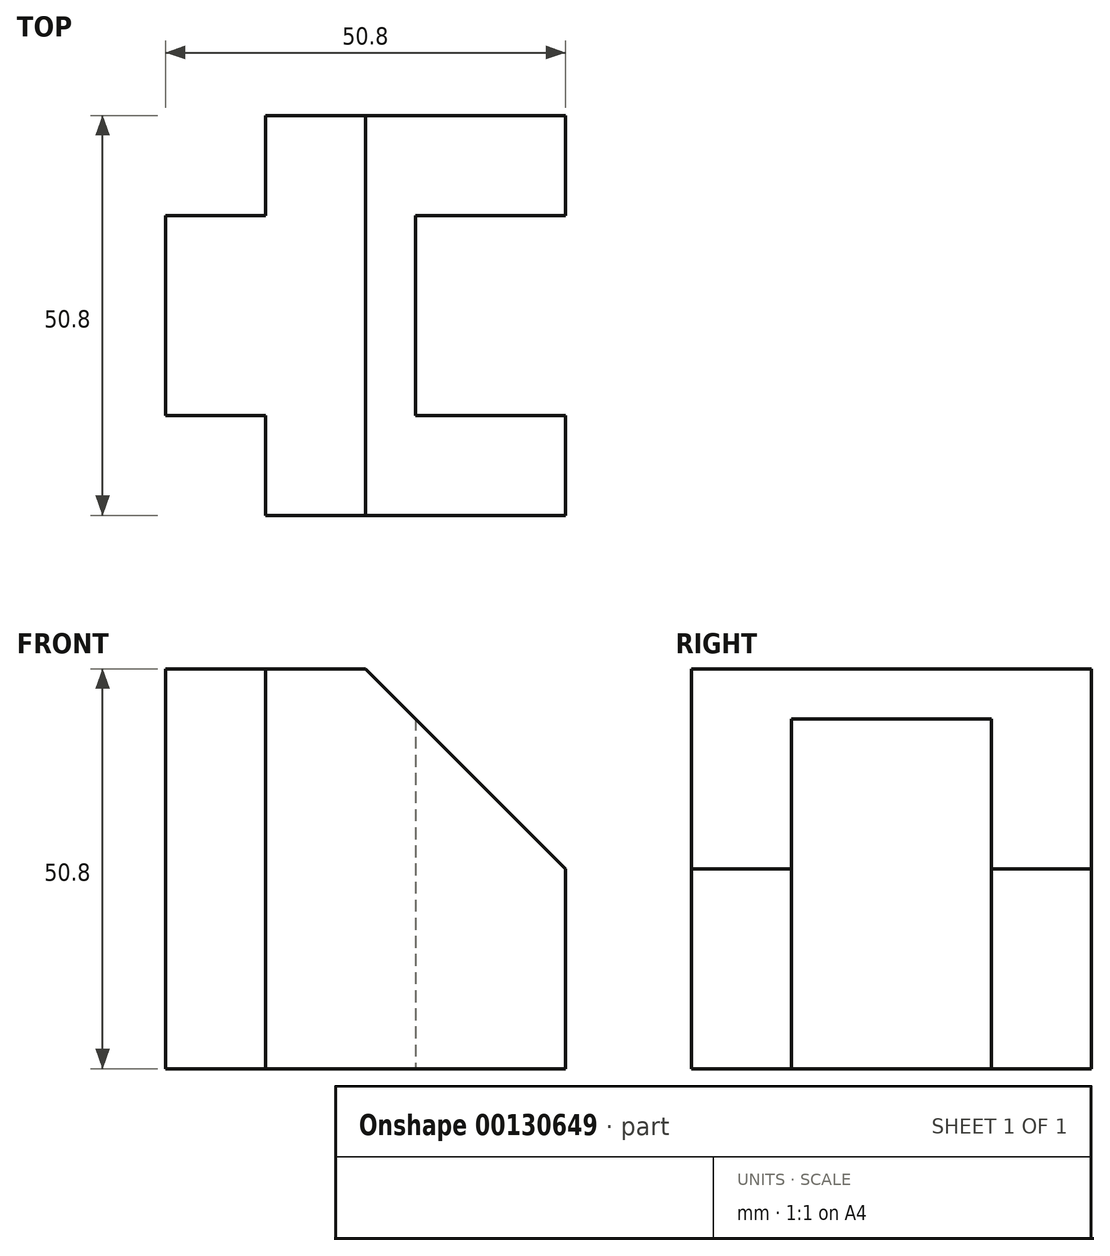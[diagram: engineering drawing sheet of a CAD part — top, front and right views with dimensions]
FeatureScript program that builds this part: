
annotation { "Feature Type Name" : "Feature", "Feature Type Description" : "" }
export const myFeature = defineFeature(function(context is Context, id is Id, definition is map)
    precondition{}
    {
        {
            var Q0;
            Q0=qCreatedBy(makeId("Front.planeOp"),FACE);
            var sketch = newSketch(context, id + "F0", { "sketchPlane" : qUnion([Q0])});
            skLineSegment(sketch, "E0", {"start": v(0, 0) * mm, "end": v(50.8, 0) * mm});
            skLineSegment(sketch, "E1", {"start": v(50.8, 0) * mm, "end": v(50.8, 25.4) * mm});
            skLineSegment(sketch, "E2", {"start": v(50.8, 25.4) * mm, "end": v(25.4, 50.8) * mm});
            skLineSegment(sketch, "E3", {"start": v(25.4, 50.8) * mm, "end": v(0, 50.8) * mm});
            skLineSegment(sketch, "E4", {"start": v(0, 50.8) * mm, "end": v(0, 0) * mm});
            skLineSegment(sketch, "E5", {"start": v(12.7, 0) * mm, "end": v(12.7, 50.8) * mm});
            skSolve(sketch);
        }
        {
            var Q0;
            {var subQ3=sQuery(id+"F0.wireOp",EDGE,"E1");Q0=makeQuery(id+"F0.imprint","IMPRINT",FACE,{"disambiguationData":[TD([[makeQuery(id+"F0.imprint","IMPRINT",EDGE,{"derivedFrom":subQ3}),1.0]])]});}
            var Q1;
            {var subQ0=sQuery(id+"F0.wireOp",EDGE,"E4");Q1=makeQuery(id+"F0.imprint","IMPRINT",FACE,{"disambiguationData":[TD([[makeQuery(id+"F0.imprint","IMPRINT",EDGE,{"derivedFrom":subQ0}),1.0]])]});}
            extrude(context, id + "F1", {"entities" : qUnion([Q0, Q1]), "endBound" : BoundingType.SYMMETRIC, "depth" : 50.8 * mm});
        }
        {
            var Q0;
            Q0=qCreatedBy(makeId("Top.planeOp"),FACE);
            var sketch = newSketch(context, id + "F2", { "sketchPlane" : qUnion([Q0])});
            skLineSegment(sketch, "E6", {"start": v(0, -25.4) * mm, "end": v(12.7, -25.4) * mm});
            skLineSegment(sketch, "E7", {"start": v(12.7, -25.4) * mm, "end": v(12.7, -12.7) * mm});
            skLineSegment(sketch, "E8", {"start": v(12.7, -12.7) * mm, "end": v(0, -12.7) * mm});
            skLineSegment(sketch, "E9", {"start": v(0, -12.7) * mm, "end": v(0, -25.4) * mm});
            skLineSegment(sketch, "E10", {"start": v(0, 25.4) * mm, "end": v(0, 12.7) * mm});
            skLineSegment(sketch, "E11", {"start": v(0, 12.7) * mm, "end": v(12.7, 12.7) * mm});
            skLineSegment(sketch, "E12", {"start": v(12.7, 12.7) * mm, "end": v(12.7, 25.4) * mm});
            skLineSegment(sketch, "E13", {"start": v(12.7, 25.4) * mm, "end": v(0, 25.4) * mm});
            skLineSegment(sketch, "E14", {"start": v(50.8, -12.7) * mm, "end": v(31.75, -12.7) * mm});
            skLineSegment(sketch, "E15", {"start": v(31.75, -12.7) * mm, "end": v(31.75, 12.7) * mm});
            skLineSegment(sketch, "E16", {"start": v(31.75, 12.7) * mm, "end": v(50.8, 12.7) * mm});
            skLineSegment(sketch, "E17", {"start": v(50.8, 12.7) * mm, "end": v(50.8, -12.7) * mm});
            skSolve(sketch);
        }
        {
            var Q0;
            Q0=makeQuery(id+"F2.imprint","IMPRINT",FACE,{"disambiguationData":[TD([[makeQuery(id+"F2.imprint","IMPRINT",EDGE,{"derivedFrom":sQuery(id+"F2.wireOp",EDGE,"E14")}),-1.0]])]});
            var Q1;
            Q1=makeQuery(id+"F2.imprint","IMPRINT",FACE,{"disambiguationData":[TD([[makeQuery(id+"F2.imprint","IMPRINT",EDGE,{"derivedFrom":sQuery(id+"F2.wireOp",EDGE,"E6")}),1.0]])]});
            var Q2;
            Q2=makeQuery(id+"F2.imprint","IMPRINT",FACE,{"disambiguationData":[TD([[makeQuery(id+"F2.imprint","IMPRINT",EDGE,{"derivedFrom":sQuery(id+"F2.wireOp",EDGE,"E10")}),1.0]])]});
            extrude(context, id + "F3", {"entities" : qUnion([Q0, Q1, Q2]), "operationType" : NewBodyOperationType.REMOVE, "endBound" : BoundingType.THROUGH_ALL, "depth" : 25.4 * mm});
        }
    });
